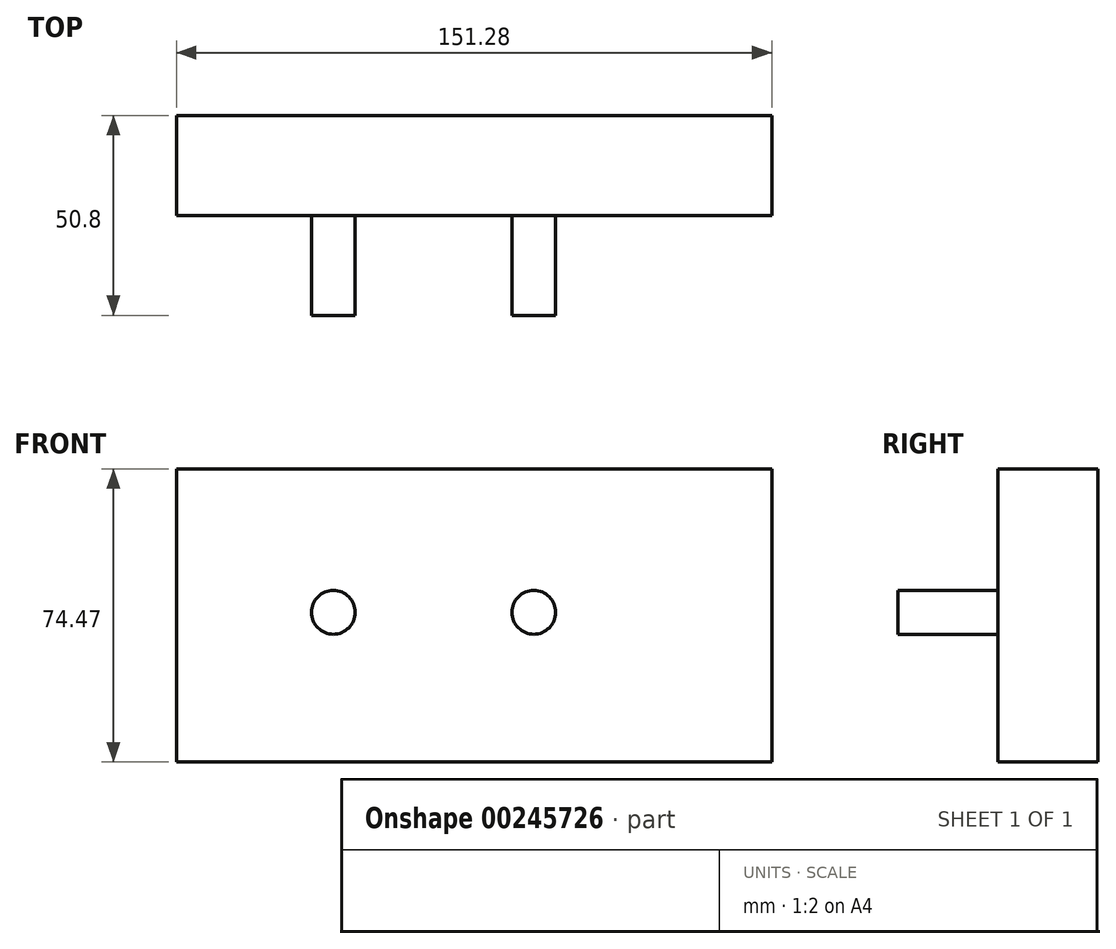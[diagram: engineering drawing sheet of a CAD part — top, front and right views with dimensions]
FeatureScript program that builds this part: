
annotation { "Feature Type Name" : "Feature", "Feature Type Description" : "" }
export const myFeature = defineFeature(function(context is Context, id is Id, definition is map)
    precondition{}
    {
        {
            var Q0;
            Q0=qCreatedBy(makeId("Front.planeOp"),FACE);
            var sketch = newSketch(context, id + "F0", { "sketchPlane" : qUnion([Q0])});
            skLineSegment(sketch, "E0.bottom", {"start": v(0, 0) * mm, "end": v(151.28, 0) * mm});
            skLineSegment(sketch, "E0.top", {"start": v(0, 74.47) * mm, "end": v(151.28, 74.47) * mm});
            skLineSegment(sketch, "E0.left", {"start": v(0, 0) * mm, "end": v(0, 74.47) * mm});
            skLineSegment(sketch, "E0.right", {"start": v(151.28, 0) * mm, "end": v(151.28, 74.47) * mm});
            skSolve(sketch);
        }
        {
            var Q0;
            Q0=makeQuery(id+"F0.imprint","IMPRINT",FACE,{"disambiguationData":[TD([[makeQuery(id+"F0.imprint","IMPRINT",EDGE,{"derivedFrom":sQuery(id+"F0.wireOp",EDGE,"E0.bottom")}),1.0]])]});
            extrude(context, id + "F1", {"entities" : qUnion([Q0]), "depth" : 25.4 * mm});
        }
        {
            var Q0;
            Q0=makeQuery(id+"F1.opExtrude","CAP_FACE",FACE,{"disambiguationData":[OSD([sQuery(id+"F0.wireOp",EDGE,"E0.bottom"),sQuery(id+"F0.wireOp",EDGE,"E0.top"),sQuery(id+"F0.wireOp",EDGE,"E0.left"),sQuery(id+"F0.wireOp",EDGE,"E0.right")])],"isStart":false});
            var sketch = newSketch(context, id + "F2", { "sketchPlane" : qUnion([Q0])});
            skCircle(sketch, "E1", {"center": v(39.87, 38.03) * mm, "radius": 5.56 * mm});
            skLineSegment(sketch, "E2", {"start": v(39.87, 38.03) * mm, "end": v(90.8, 38.03) * mm, "construction": true});
            skCircle(sketch, "E3", {"center": v(90.8, 38.03) * mm, "radius": 5.56 * mm});
            skSolve(sketch);
        }
        {
            var Q0;
            Q0=makeQuery(id+"F2.imprint","IMPRINT",FACE,{"disambiguationData":[TD([[makeQuery(id+"F2.imprint","IMPRINT",EDGE,{"derivedFrom":sQuery(id+"F2.wireOp",EDGE,"E1")}),1.0]])]});
            var Q1;
            Q1=makeQuery(id+"F2.imprint","IMPRINT",FACE,{"disambiguationData":[TD([[makeQuery(id+"F2.imprint","IMPRINT",EDGE,{"derivedFrom":sQuery(id+"F2.wireOp",EDGE,"E3")}),1.0]])]});
            extrude(context, id + "F3", {"entities" : qUnion([Q0, Q1]), "operationType" : NewBodyOperationType.ADD, "depth" : 25.4 * mm});
        }
    });
